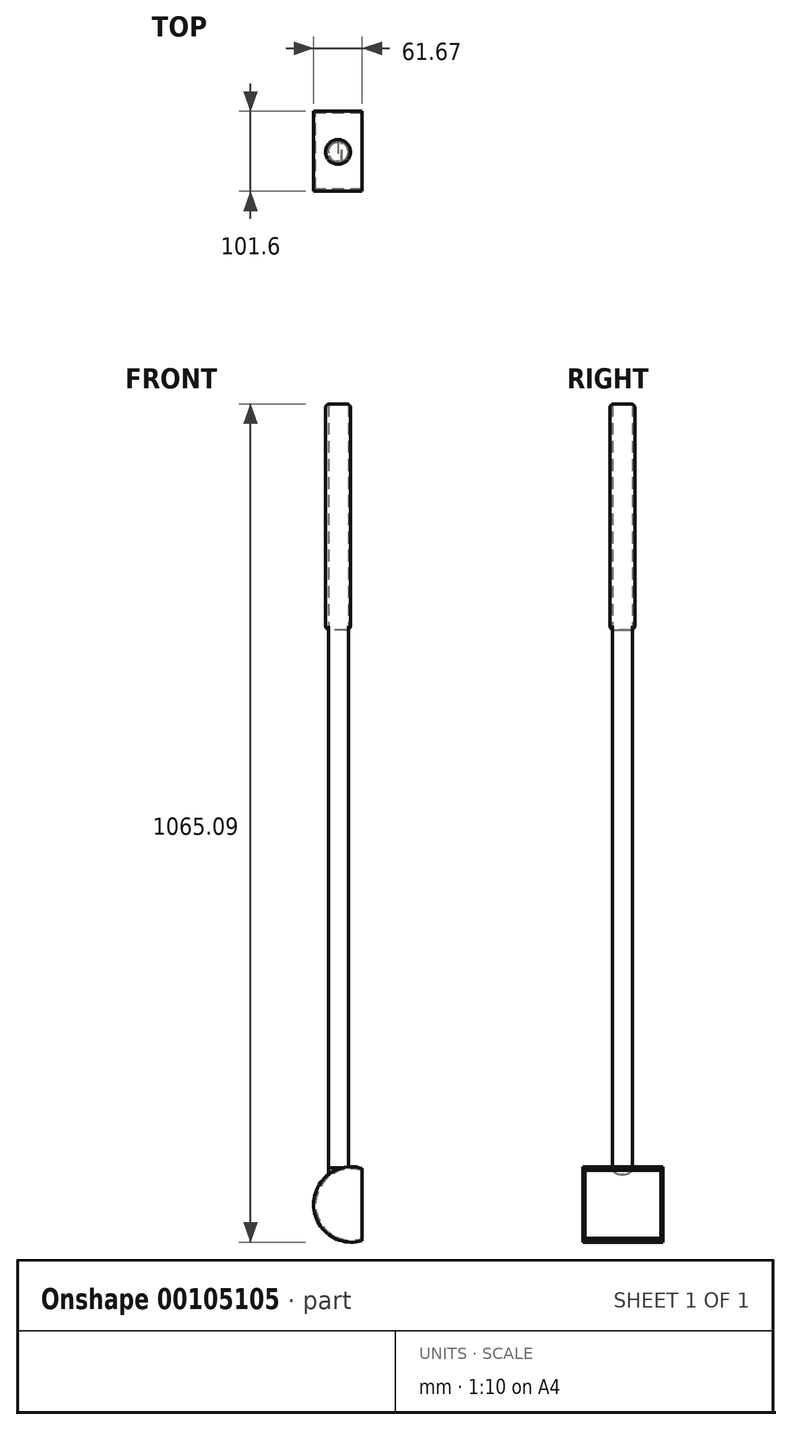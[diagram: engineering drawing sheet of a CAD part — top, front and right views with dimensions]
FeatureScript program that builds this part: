
annotation { "Feature Type Name" : "Feature", "Feature Type Description" : "" }
export const myFeature = defineFeature(function(context is Context, id is Id, definition is map)
    precondition{}
    {
        {
            var Q0;
            Q0=qCreatedBy(makeId("Front.planeOp"),FACE);
            var sketch = newSketch(context, id + "F0", { "sketchPlane" : qUnion([Q0])});
            skArc(sketch, "E0", {"start": v(0, 45.92) * mm, "mid": v(-61.67, 0) * mm, "end": v(0, -45.92) * mm});
            skLineSegment(sketch, "E1", {"start": v(0, 45.92) * mm, "end": v(0, -45.92) * mm});
            skSolve(sketch);
        }
        {
            var Q0;
            Q0 = qSketchRegion(id + "F0", true);
            extrude(context, id + "F1", {"entities" : qUnion([Q0]), "depth" : 101.6 * mm});
        }
        {
            var Q0;
            Q0=makeQuery(id+"F1.opExtrude","SWEPT_FACE",FACE,{"disambiguationData":[OSD([sQuery(id+"F0.wireOp",EDGE,"E1")])]});
            shell(context, id + "F2", {"entities" : qUnion([Q0]), "thickness" : 2.54 * mm});
        }
        {
            var Q0;
            Q0=qCreatedBy(makeId("Top.planeOp"),FACE);
            var sketch = newSketch(context, id + "F3", { "sketchPlane" : qUnion([Q0])});
            skCircle(sketch, "E2", {"center": v(-30.24, -51.68) * mm, "radius": 12.7 * mm});
            skSolve(sketch);
        }
        {
            var Q0;
            Q0 = qSketchRegion(id + "F3", true);
            extrude(context, id + "F4", {"entities" : qUnion([Q0]), "operationType" : NewBodyOperationType.ADD, "depth" : 1016 * mm, "hasSecondDirection" : true, "secondDirectionOppositeDirection" : false, "secondDirectionDepth" : 46.38 * mm});
        }
        {
            var Q0;
            Q0=qCreatedBy(makeId("Front.planeOp"),FACE);
            var sketch = newSketch(context, id + "F5", { "sketchPlane" : qUnion([Q0])});
            skLineSegment(sketch, "E3", {"start": v(-42.95, 46.44) * mm, "end": v(-42.95, 38.01) * mm});
            skLineSegment(sketch, "E4", {"start": v(-42.95, 38.01) * mm, "end": v(-25.9, 46.35) * mm});
            skLineSegment(sketch, "E5", {"start": v(-25.9, 46.35) * mm, "end": v(-42.95, 46.44) * mm});
            skSolve(sketch);
        }
        {
            var Q0;
            Q0 = qSketchRegion(id + "F5", true);
            extrude(context, id + "F6", {"entities" : qUnion([Q0]), "operationType" : NewBodyOperationType.ADD, "depth" : 64.64 * mm, "hasSecondDirection" : true, "secondDirectionOppositeDirection" : false, "secondDirectionDepth" : 39 * mm});
        }
        {
            var Q0;
            Q0=makeQuery(id+"F6.opExtrude","CAP_EDGE",EDGE,{"disambiguationData":[OSD([sQuery(id+"F5.wireOp",EDGE,"E3")])],"isStart":false});
            var Q1;
            Q1=makeQuery(id+"F6.opExtrude","CAP_EDGE",EDGE,{"disambiguationData":[OSD([sQuery(id+"F5.wireOp",EDGE,"E3")])],"isStart":true});
            fillet(context, id + "F7", {"entities" : qUnion([Q0, Q1]), "radius" : 12.07 * mm, "tangentPropagation" : true, "allowEdgeOverflow" : false});
        }
        {
            var Q0;
            Q0=qCreatedBy(makeId("Top.planeOp"),FACE);
            var sketch = newSketch(context, id + "F8", { "sketchPlane" : qUnion([Q0])});
            skCircle(sketch, "E6", {"center": v(-30.66, -51.65) * mm, "radius": 15.74 * mm});
            skSolve(sketch);
        }
        {
            var Q0;
            Q0 = qSketchRegion(id + "F8", true);
            extrude(context, id + "F9", {"entities" : qUnion([Q0]), "depth" : 1017.16 * mm, "hasSecondDirection" : true, "secondDirectionOppositeDirection" : false, "secondDirectionDepth" : 729.95 * mm});
        }
        {
            var Q0;
            Q0=makeQuery(id+"F9.opExtrude","CAP_EDGE",EDGE,{"disambiguationData":[OSD([sQuery(id+"F8.wireOp",EDGE,"E6")])],"isStart":true});
            var Q1;
            Q1=makeQuery(id+"F9.opExtrude","CAP_EDGE",EDGE,{"disambiguationData":[OSD([sQuery(id+"F8.wireOp",EDGE,"E6")])],"isStart":false});
            fillet(context, id + "F10", {"entities" : qUnion([Q0, Q1]), "radius" : 5.08 * mm, "tangentPropagation" : true, "allowEdgeOverflow" : false});
        }
    });
